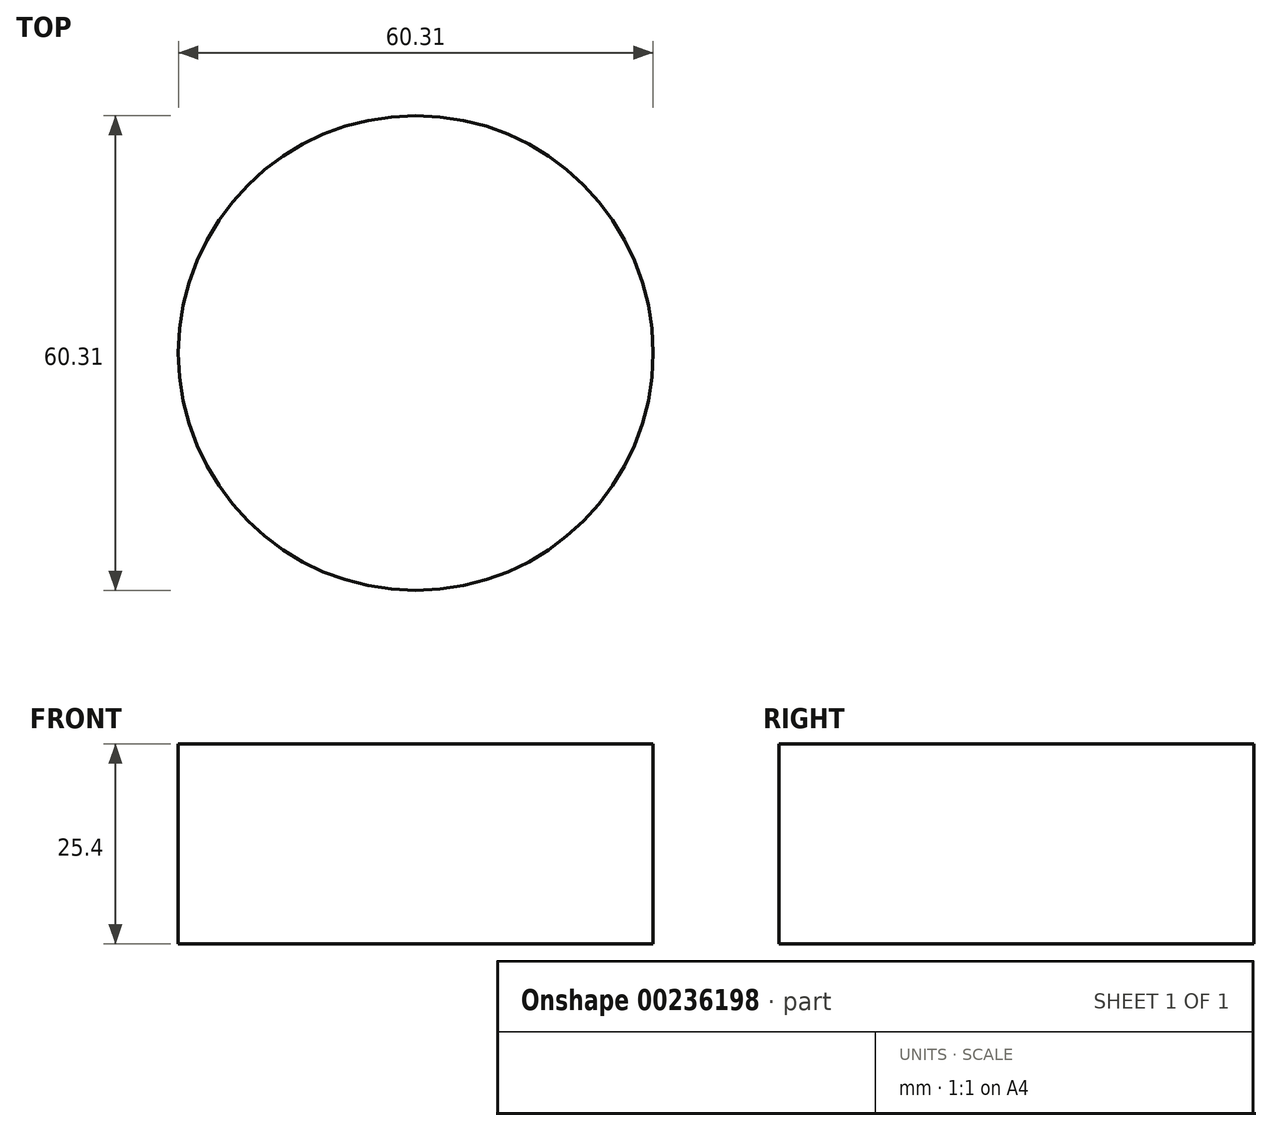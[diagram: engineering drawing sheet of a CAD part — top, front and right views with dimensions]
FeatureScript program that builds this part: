
annotation { "Feature Type Name" : "Feature", "Feature Type Description" : "" }
export const myFeature = defineFeature(function(context is Context, id is Id, definition is map)
    precondition{}
    {
        {
            var Q0;
            Q0=qCreatedBy(makeId("Top.planeOp"),FACE);
            var sketch = newSketch(context, id + "F0", { "sketchPlane" : qUnion([Q0])});
            skCircle(sketch, "E0", {"center": v(-40.16, -14.9) * mm, "radius": 30.16 * mm});
            skSolve(sketch);
        }
        {
            var Q0;
            Q0=makeQuery(id+"F0.imprint","IMPRINT",FACE,{"disambiguationData":[TD([[makeQuery(id+"F0.imprint","IMPRINT",EDGE,{"derivedFrom":sQuery(id+"F0.wireOp",EDGE,"E0")}),1.0]])]});
            extrude(context, id + "F1", {"entities" : qUnion([Q0]), "depth" : 25.4 * mm});
        }
    });
